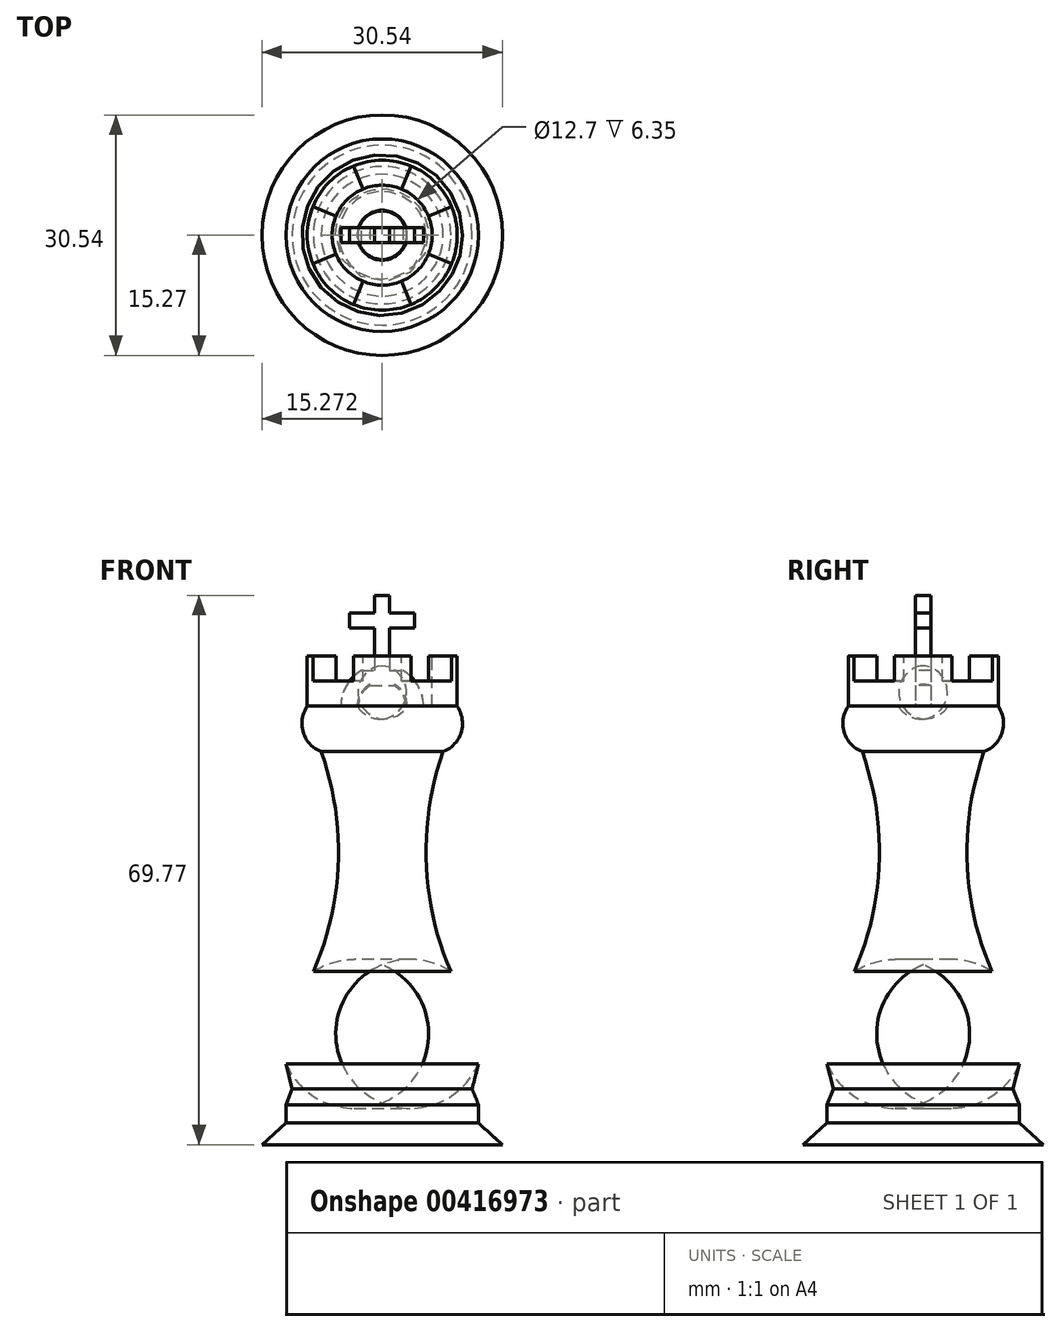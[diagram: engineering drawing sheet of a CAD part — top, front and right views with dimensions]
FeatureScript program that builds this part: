
annotation { "Feature Type Name" : "Feature", "Feature Type Description" : "" }
export const myFeature = defineFeature(function(context is Context, id is Id, definition is map)
    precondition{}
    {
        {
            var Q0;
            Q0=qCreatedBy(makeId("Front.planeOp"),FACE);
            var sketch = newSketch(context, id + "F0", { "sketchPlane" : qUnion([Q0])});
            skArc(sketch, "E0", {"start": v(0.91, 15.92) * mm, "mid": v(-1.24, 1.86) * mm, "end": v(1.91, -12.01) * mm});
            skArc(sketch, "E1", {"start": v(0.91, 15.92) * mm, "mid": v(3.2, 18.37) * mm, "end": v(2.7, 21.7) * mm});
            skLineSegment(sketch, "E2", {"start": v(2.7, 21.7) * mm, "end": v(2.7, 28.04) * mm});
            skLineSegment(sketch, "E3", {"start": v(2.7, 28.04) * mm, "end": v(-0.48, 28.04) * mm});
            skLineSegment(sketch, "E4", {"start": v(-0.48, 28.04) * mm, "end": v(-0.48, 21.7) * mm});
            skLineSegment(sketch, "E5", {"start": v(-0.48, 21.7) * mm, "end": v(-3.65, 21.7) * mm});
            skLineSegment(sketch, "E6", {"start": v(-6.83, 21.7) * mm, "end": v(-6.83, -12.01) * mm});
            skLineSegment(sketch, "E7", {"start": v(-6.83, -12.01) * mm, "end": v(1.91, -12.01) * mm});
            skArc(sketch, "E8", {"start": v(5.4, -23.75) * mm, "mid": v(5.8, -17.24) * mm, "end": v(1.91, -12.01) * mm});
            skLineSegment(sketch, "E9", {"start": v(5.4, -23.75) * mm, "end": v(4.6, -26.91) * mm});
            skLineSegment(sketch, "E10", {"start": v(4.6, -26.91) * mm, "end": v(5.4, -28.94) * mm});
            skLineSegment(sketch, "E11", {"start": v(5.4, -28.94) * mm, "end": v(5.4, -31.26) * mm});
            skLineSegment(sketch, "E12", {"start": v(5.4, -31.26) * mm, "end": v(8.44, -34) * mm});
            skLineSegment(sketch, "E13", {"start": v(8.44, -34) * mm, "end": v(-6.83, -34) * mm});
            skLineSegment(sketch, "E14", {"start": v(-6.83, -34) * mm, "end": v(-6.83, -12.01) * mm});
            skArc(sketch, "E15", {"start": v(-6.83, 20.1) * mm, "mid": v(-5.01, 20.44) * mm, "end": v(-3.65, 21.7) * mm});
            skSolve(sketch);
        }
        {
            var Q0;
            Q0=qSketchRegion(id+"F0",true);
            var Q1;
            Q1=sQuery(id+"F0.wireOp",EDGE,"E6");
            revolve(context, id + "F1", {"entities" : qUnion([Q0]), "axis" : qUnion([Q1]), "revolveType" : RevolveType.FULL});
        }
        {
            var Q0;
            Q0=makeQuery(id+"F1.opRevolve","SWEPT_FACE",FACE,{"disambiguationData":[OSD([sQuery(id+"F0.wireOp",EDGE,"E3")])]});
            var sketch = newSketch(context, id + "F2", { "sketchPlane" : qUnion([Q0])});
            skCircle(sketch, "E16", {"center": v(-6.83, 0) * mm, "radius": 9.53 * mm});
            skCircle(sketch, "E17", {"center": v(-6.83, 0) * mm, "radius": 6.35 * mm});
            skLineSegment(sketch, "E18", {"start": v(-6.83, 0) * mm, "end": v(-6.83, 9.53) * mm});
            skLineSegment(sketch, "E19", {"start": v(-6.83, 0) * mm, "end": v(-6.83, -9.53) * mm});
            skLineSegment(sketch, "E20", {"start": v(-6.83, 0) * mm, "end": v(2.7, 0) * mm});
            skLineSegment(sketch, "E21", {"start": v(-6.83, 0) * mm, "end": v(-16.35, 0) * mm});
            skLineSegment(sketch, "E22", {"start": v(-6.83, 0) * mm, "end": v(-15.63, 3.65) * mm});
            skLineSegment(sketch, "E23", {"start": v(-6.83, 0) * mm, "end": v(-10.47, 8.8) * mm});
            skLineSegment(sketch, "E24", {"start": v(-6.83, 0) * mm, "end": v(-13.56, 6.74) * mm});
            skLineSegment(sketch, "E25", {"start": v(-6.83, 0) * mm, "end": v(-3.18, 8.8) * mm});
            skLineSegment(sketch, "E26", {"start": v(-6.83, 0) * mm, "end": v(-0.1, 6.74) * mm});
            skLineSegment(sketch, "E27", {"start": v(-6.83, 0) * mm, "end": v(1.97, 3.65) * mm});
            skLineSegment(sketch, "E28", {"start": v(-6.83, 0) * mm, "end": v(1.97, -3.65) * mm});
            skLineSegment(sketch, "E29", {"start": v(-6.83, 0) * mm, "end": v(-0.1, -6.74) * mm});
            skLineSegment(sketch, "E30", {"start": v(-6.83, 0) * mm, "end": v(-3.18, -8.8) * mm});
            skLineSegment(sketch, "E31", {"start": v(-6.83, 0) * mm, "end": v(-10.47, -8.8) * mm});
            skLineSegment(sketch, "E32", {"start": v(-6.83, 0) * mm, "end": v(-13.56, -6.74) * mm});
            skLineSegment(sketch, "E33", {"start": v(-6.83, 0) * mm, "end": v(-15.63, -3.65) * mm});
            skSolve(sketch);
        }
        {
            var Q0;
            {var subQ0=sQuery(id+"F2.wireOp",EDGE,"E23");var subQ1=sQuery(id+"F2.wireOp",EDGE,"E16");var subQ2=makeQuery(id+"F2.imprint","INTERSECT",VERTEX,{"derivedFrom":[subQ1,subQ0]});Q0=makeQuery(id+"F2.imprint","IMPRINT",FACE,{"disambiguationData":[TD([[makeQuery(id+"F2.imprint","IMPRINT",EDGE,{"disambiguationData":[TD([[subQ2,-1.0]])],"derivedFrom":subQ1}),1.0]])]});}
            var Q1;
            {var subQ0=sQuery(id+"F2.wireOp",EDGE,"E22");var subQ1=sQuery(id+"F2.wireOp",EDGE,"E16");var subQ2=makeQuery(id+"F2.imprint","INTERSECT",VERTEX,{"derivedFrom":[subQ1,subQ0]});Q1=makeQuery(id+"F2.imprint","IMPRINT",FACE,{"disambiguationData":[TD([[makeQuery(id+"F2.imprint","IMPRINT",EDGE,{"disambiguationData":[TD([[subQ2,1.0]])],"derivedFrom":subQ1}),1.0]])]});}
            var Q2;
            {var subQ0=sQuery(id+"F2.wireOp",EDGE,"E25");var subQ1=sQuery(id+"F2.wireOp",EDGE,"E16");var subQ2=makeQuery(id+"F2.imprint","INTERSECT",VERTEX,{"derivedFrom":[subQ1,subQ0]});Q2=makeQuery(id+"F2.imprint","IMPRINT",FACE,{"disambiguationData":[TD([[makeQuery(id+"F2.imprint","IMPRINT",EDGE,{"disambiguationData":[TD([[subQ2,1.0]])],"derivedFrom":subQ1}),1.0]])]});}
            var Q3;
            {var subQ0=sQuery(id+"F2.wireOp",EDGE,"E26");var subQ1=sQuery(id+"F2.wireOp",EDGE,"E16");var subQ2=makeQuery(id+"F2.imprint","INTERSECT",VERTEX,{"derivedFrom":[subQ1,subQ0]});Q3=makeQuery(id+"F2.imprint","IMPRINT",FACE,{"disambiguationData":[TD([[makeQuery(id+"F2.imprint","IMPRINT",EDGE,{"disambiguationData":[TD([[subQ2,1.0]])],"derivedFrom":subQ1}),1.0]])]});}
            var Q4;
            {var subQ0=sQuery(id+"F2.wireOp",EDGE,"E28");var subQ1=sQuery(id+"F2.wireOp",EDGE,"E16");var subQ2=makeQuery(id+"F2.imprint","INTERSECT",VERTEX,{"derivedFrom":[subQ1,subQ0]});Q4=makeQuery(id+"F2.imprint","IMPRINT",FACE,{"disambiguationData":[TD([[makeQuery(id+"F2.imprint","IMPRINT",EDGE,{"disambiguationData":[TD([[subQ2,1.0]])],"derivedFrom":subQ1}),1.0]])]});}
            var Q5;
            {var subQ0=sQuery(id+"F2.wireOp",EDGE,"E29");var subQ1=sQuery(id+"F2.wireOp",EDGE,"E16");var subQ2=makeQuery(id+"F2.imprint","INTERSECT",VERTEX,{"derivedFrom":[subQ1,subQ0]});Q5=makeQuery(id+"F2.imprint","IMPRINT",FACE,{"disambiguationData":[TD([[makeQuery(id+"F2.imprint","IMPRINT",EDGE,{"disambiguationData":[TD([[subQ2,1.0]])],"derivedFrom":subQ1}),1.0]])]});}
            var Q6;
            {var subQ0=sQuery(id+"F2.wireOp",EDGE,"E31");var subQ1=sQuery(id+"F2.wireOp",EDGE,"E16");var subQ2=makeQuery(id+"F2.imprint","INTERSECT",VERTEX,{"derivedFrom":[subQ1,subQ0]});Q6=makeQuery(id+"F2.imprint","IMPRINT",FACE,{"disambiguationData":[TD([[makeQuery(id+"F2.imprint","IMPRINT",EDGE,{"disambiguationData":[TD([[subQ2,1.0]])],"derivedFrom":subQ1}),1.0]])]});}
            var Q7;
            {var subQ0=sQuery(id+"F2.wireOp",EDGE,"E32");var subQ1=sQuery(id+"F2.wireOp",EDGE,"E16");var subQ2=makeQuery(id+"F2.imprint","INTERSECT",VERTEX,{"derivedFrom":[subQ1,subQ0]});Q7=makeQuery(id+"F2.imprint","IMPRINT",FACE,{"disambiguationData":[TD([[makeQuery(id+"F2.imprint","IMPRINT",EDGE,{"disambiguationData":[TD([[subQ2,1.0]])],"derivedFrom":subQ1}),1.0]])]});}
            extrude(context, id + "F3", {"entities" : qUnion([Q0, Q1, Q2, Q3, Q4, Q5, Q6, Q7]), "operationType" : NewBodyOperationType.REMOVE, "oppositeDirection" : true, "depth" : 3.17 * mm, "offsetDistance" : 25.4 * mm});
        }
        {
            var Q0;
            Q0=makeQuery(id+"F1.opRevolve","SWEPT_FACE",FACE,{"disambiguationData":[OSD([sQuery(id+"F0.wireOp",EDGE,"E5")])]});
            var sketch = newSketch(context, id + "F4", { "sketchPlane" : qUnion([Q0])});
            skLineSegment(sketch, "E34", {"start": v(-12.08, 0) * mm, "end": v(-12.08, 0.95) * mm});
            skLineSegment(sketch, "E35", {"start": v(-12.08, 0.95) * mm, "end": v(-9.86, 0.95) * mm});
            skLineSegment(sketch, "E36", {"start": v(-12.08, 0) * mm, "end": v(-12.08, -0.95) * mm});
            skLineSegment(sketch, "E37", {"start": v(-12.08, -0.95) * mm, "end": v(-9.86, -0.95) * mm});
            skLineSegment(sketch, "E38", {"start": v(-1.58, 0.95) * mm, "end": v(-1.58, 0) * mm});
            skLineSegment(sketch, "E39", {"start": v(-1.58, 0) * mm, "end": v(-1.58, -0.95) * mm});
            skLineSegment(sketch, "E40", {"start": v(-1.58, -0.95) * mm, "end": v(-3.8, -0.95) * mm});
            skLineSegment(sketch, "E41", {"start": v(-1.58, 0.95) * mm, "end": v(-3.8, 0.95) * mm});
            skCircle(sketch, "E42", {"center": v(-6.83, 0) * mm, "radius": 3.18 * mm});
            skLineSegment(sketch, "E43", {"start": v(-6.83, 0) * mm, "end": v(-6.83, 1.77) * mm});
            skLineSegment(sketch, "E44", {"start": v(-6.83, 0) * mm, "end": v(-6.83, -1.33) * mm});
            skSolve(sketch);
        }
        {
            var Q0;
            Q0=makeQuery(id+"F4.imprint","IMPRINT",FACE,{"disambiguationData":[TD([[makeQuery(id+"F4.imprint","IMPRINT",EDGE,{"derivedFrom":sQuery(id+"F4.wireOp",EDGE,"E34")}),-1.0]])]});
            var Q1;
            Q1=sQuery(id+"F4.wireOp",EDGE,"E43");
            revolve(context, id + "F5", {"operationType" : NewBodyOperationType.ADD, "entities" : qUnion([Q0]), "axis" : qUnion([Q1]), "revolveType" : RevolveType.ONE_DIRECTION, "angle" : 60 * degree});
        }
        {
            var Q0;
            Q0=makeQuery(id+"F4.imprint","IMPRINT",FACE,{"disambiguationData":[TD([[makeQuery(id+"F4.imprint","IMPRINT",EDGE,{"derivedFrom":sQuery(id+"F4.wireOp",EDGE,"E38")}),-1.0]])]});
            var Q1;
            Q1=sQuery(id+"F4.wireOp",EDGE,"E43");
            revolve(context, id + "F6", {"operationType" : NewBodyOperationType.ADD, "entities" : qUnion([Q0]), "axis" : qUnion([Q1]), "revolveType" : RevolveType.ONE_DIRECTION, "oppositeDirection" : true, "angle" : 60 * degree});
        }
        {
            var Q0;
            Q0=makeQuery(id+"F5.opRevolve","SWEPT_FACE",FACE,{"disambiguationData":[OSD([sQuery(id+"F4.wireOp",EDGE,"E37")])]});
            var sketch = newSketch(context, id + "F7", { "sketchPlane" : qUnion([Q0])});
            skLineSegment(sketch, "E45", {"start": v(-9.45, 26.24) * mm, "end": v(-4.2, 26.24) * mm});
            skLineSegment(sketch, "E46", {"start": v(-8.34, 24.31) * mm, "end": v(-5.31, 24.31) * mm});
            skLineSegment(sketch, "E47", {"start": v(-9.45, 26.24) * mm, "end": v(-8.34, 24.31) * mm});
            skLineSegment(sketch, "E48", {"start": v(-4.2, 26.24) * mm, "end": v(-5.31, 24.31) * mm});
            skSolve(sketch);
        }
        {
            var Q0;
            Q0 = qSketchRegion(id + "F7", true);
            extrude(context, id + "F8", {"entities" : qUnion([Q0]), "operationType" : NewBodyOperationType.ADD, "oppositeDirection" : true, "depth" : 1.9 * mm, "offsetDistance" : 25.4 * mm});
        }
        {
            var Q0;
            Q0=makeQuery(id+"F8.opExtrude","SWEPT_FACE",FACE,{"disambiguationData":[OSD([sQuery(id+"F7.wireOp",EDGE,"E45")])]});
            var sketch = newSketch(context, id + "F9", { "sketchPlane" : qUnion([Q0])});
            skLineSegment(sketch, "E49.bottom", {"start": v(-7.78, 0.95) * mm, "end": v(-5.88, 0.95) * mm});
            skLineSegment(sketch, "E49.top", {"start": v(-7.78, -0.95) * mm, "end": v(-5.88, -0.95) * mm});
            skLineSegment(sketch, "E49.left", {"start": v(-7.78, 0.95) * mm, "end": v(-7.78, -0.95) * mm});
            skLineSegment(sketch, "E49.right", {"start": v(-5.88, 0.95) * mm, "end": v(-5.88, -0.95) * mm});
            skPoint(sketch, "E49.middle", {"position": v(-6.83, 0) * mm});
            skPoint(sketch, "E49.middle.positionSnap0", {"position": v(-6.83, -0.95) * mm});
            skPoint(sketch, "E49.centerSnap0", {"position": v(-6.83, -0.95) * mm});
            skSolve(sketch);
        }
        {
            var Q0;
            Q0 = qSketchRegion(id + "F9", true);
            extrude(context, id + "F10", {"entities" : qUnion([Q0]), "operationType" : NewBodyOperationType.ADD, "depth" : 9.52 * mm, "offsetDistance" : 25.4 * mm});
        }
        {
            var Q0;
            Q0=makeQuery(id+"F10.opExtrude","SWEPT_FACE",FACE,{"disambiguationData":[OSD([sQuery(id+"F9.wireOp",EDGE,"E49.right")])]});
            var sketch = newSketch(context, id + "F11", { "sketchPlane" : qUnion([Q0])});
            skLineSegment(sketch, "E50.bottom", {"start": v(-0.95, 31.64) * mm, "end": v(0.95, 31.64) * mm});
            skLineSegment(sketch, "E50.top", {"start": v(-0.95, 33.54) * mm, "end": v(0.95, 33.54) * mm});
            skLineSegment(sketch, "E50.left", {"start": v(-0.95, 31.64) * mm, "end": v(-0.95, 33.54) * mm});
            skLineSegment(sketch, "E50.right", {"start": v(0.95, 31.64) * mm, "end": v(0.95, 33.54) * mm});
            skPoint(sketch, "E50.middle", {"position": v(0, 32.59) * mm});
            skSolve(sketch);
        }
        {
            var Q0;
            Q0=makeQuery(id+"F10.opExtrude","SWEPT_FACE",FACE,{"disambiguationData":[OSD([sQuery(id+"F9.wireOp",EDGE,"E49.left")])]});
            var sketch = newSketch(context, id + "F12", { "sketchPlane" : qUnion([Q0])});
            skLineSegment(sketch, "E51.bottom", {"start": v(-0.95, 33.54) * mm, "end": v(0.95, 33.54) * mm});
            skLineSegment(sketch, "E51.top", {"start": v(-0.95, 31.64) * mm, "end": v(0.95, 31.64) * mm});
            skLineSegment(sketch, "E51.left", {"start": v(-0.95, 33.54) * mm, "end": v(-0.95, 31.64) * mm});
            skLineSegment(sketch, "E51.right", {"start": v(0.95, 33.54) * mm, "end": v(0.95, 31.64) * mm});
            skPoint(sketch, "E51.middle", {"position": v(0, 32.59) * mm});
            skSolve(sketch);
        }
        {
            var Q0;
            Q0=makeQuery(id+"F12.imprint","IMPRINT",FACE,{"disambiguationData":[TD([[makeQuery(id+"F12.imprint","IMPRINT",EDGE,{"derivedFrom":sQuery(id+"F12.wireOp",EDGE,"E51.bottom")}),-1.0]])]});
            extrude(context, id + "F13", {"entities" : qUnion([Q0]), "operationType" : NewBodyOperationType.ADD, "depth" : 3.17 * mm, "offsetDistance" : 25.4 * mm});
        }
        {
            var Q0;
            Q0=makeQuery(id+"F11.imprint","IMPRINT",FACE,{"disambiguationData":[TD([[makeQuery(id+"F11.imprint","IMPRINT",EDGE,{"derivedFrom":sQuery(id+"F11.wireOp",EDGE,"E50.bottom")}),1.0]])]});
            extrude(context, id + "F14", {"entities" : qUnion([Q0]), "operationType" : NewBodyOperationType.ADD, "depth" : 3.17 * mm, "offsetDistance" : 25.4 * mm});
        }
    });
